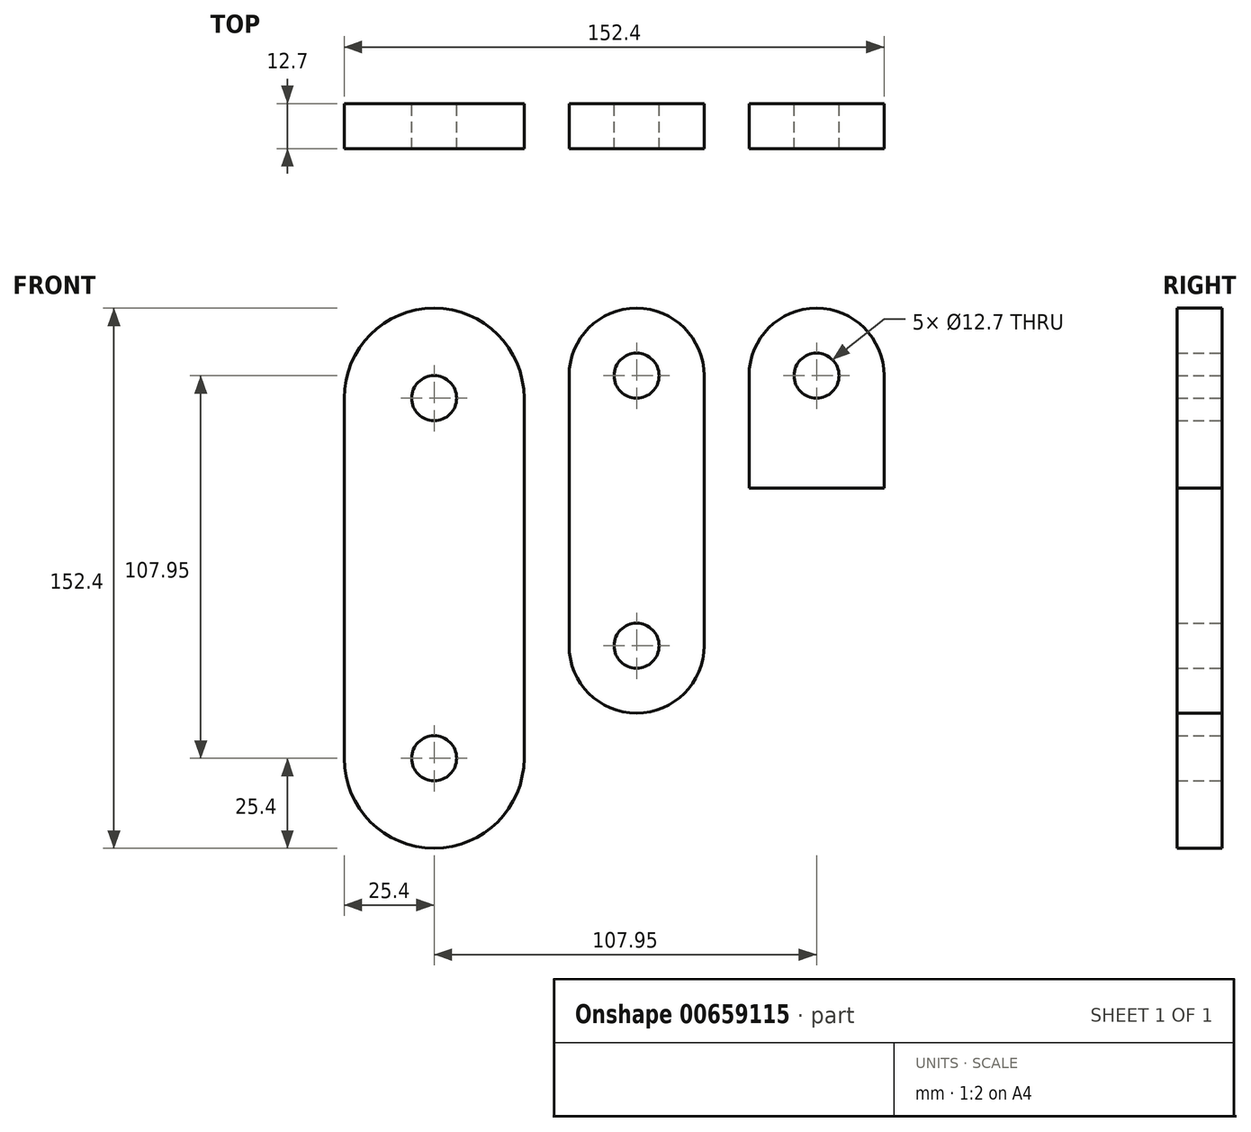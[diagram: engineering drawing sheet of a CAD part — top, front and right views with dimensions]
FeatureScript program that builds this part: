
annotation { "Feature Type Name" : "Feature", "Feature Type Description" : "" }
export const myFeature = defineFeature(function(context is Context, id is Id, definition is map)
    precondition{}
    {
        {
            var Q0;
            Q0=qCreatedBy(makeId("Front.planeOp"),FACE);
            var sketch = newSketch(context, id + "F0", { "sketchPlane" : qUnion([Q0])});
            skArc(sketch, "E0", {"start": v(19.05, 31.75) * mm, "mid": v(0, 50.8) * mm, "end": v(-19.05, 31.75) * mm});
            skCircle(sketch, "E1", {"center": v(0, 31.75) * mm, "radius": 6.35 * mm});
            skLineSegment(sketch, "E2", {"start": v(19.05, 31.75) * mm, "end": v(19.05, 0) * mm});
            skLineSegment(sketch, "E3", {"start": v(-19.05, 0) * mm, "end": v(19.05, 0) * mm});
            skPoint(sketch, "E4.start.orphan", {"position": v(-19.05, 63.5) * mm});
            skPoint(sketch, "E5.center.orphan", {"position": v(0, -25.4) * mm});
            skLineSegment(sketch, "E6", {"start": v(-19.05, 31.75) * mm, "end": v(-19.05, 0) * mm});
            skSolve(sketch);
        }
        {
            var Q0;
            Q0 = qSketchRegion(id + "F0", true);
            extrude(context, id + "F1", {"entities" : qUnion([Q0]), "depth" : 12.7 * mm, "offsetDistance" : 25.4 * mm});
        }
        {
            var Q0;
            Q0=qCreatedBy(makeId("Front.planeOp"),FACE);
            var sketch = newSketch(context, id + "F2", { "sketchPlane" : qUnion([Q0])});
            skCircle(sketch, "E7", {"center": v(-50.8, 31.75) * mm, "radius": 6.35 * mm});
            skArc(sketch, "E8", {"start": v(-31.75, 31.75) * mm, "mid": v(-50.8, 50.8) * mm, "end": v(-69.85, 31.75) * mm});
            skCircle(sketch, "E9", {"center": v(-50.8, -44.45) * mm, "radius": 6.35 * mm});
            skArc(sketch, "E10", {"start": v(-69.85, -44.45) * mm, "mid": v(-50.8, -63.5) * mm, "end": v(-31.75, -44.45) * mm});
            skLineSegment(sketch, "E11", {"start": v(-69.85, 31.75) * mm, "end": v(-69.85, -44.45) * mm});
            skLineSegment(sketch, "E12", {"start": v(-31.75, 31.75) * mm, "end": v(-31.75, -44.45) * mm});
            skSolve(sketch);
        }
        {
            var Q0;
            Q0 = qSketchRegion(id + "F2", true);
            extrude(context, id + "F3", {"entities" : qUnion([Q0]), "depth" : 12.7 * mm, "offsetDistance" : 25.4 * mm});
        }
        {
            var Q0;
            Q0=qCreatedBy(makeId("Front.planeOp"),FACE);
            var sketch = newSketch(context, id + "F4", { "sketchPlane" : qUnion([Q0])});
            skCircle(sketch, "E13", {"center": v(-107.95, 25.4) * mm, "radius": 6.35 * mm});
            skCircle(sketch, "E14", {"center": v(-107.95, -76.2) * mm, "radius": 6.35 * mm});
            skArc(sketch, "E15", {"start": v(-82.55, 25.4) * mm, "mid": v(-107.95, 50.8) * mm, "end": v(-133.35, 25.4) * mm});
            skArc(sketch, "E16", {"start": v(-133.35, -76.2) * mm, "mid": v(-107.95, -101.6) * mm, "end": v(-82.55, -76.2) * mm});
            skLineSegment(sketch, "E17", {"start": v(-133.35, 25.4) * mm, "end": v(-133.35, -76.2) * mm});
            skLineSegment(sketch, "E18", {"start": v(-82.55, 25.4) * mm, "end": v(-82.55, -76.2) * mm});
            skLineSegment(sketch, "E19", {"start": v(-107.95, 50.8) * mm, "end": v(-77.73, 50.8) * mm, "construction": true});
            skSolve(sketch);
        }
        {
            var Q0;
            Q0 = qSketchRegion(id + "F4", true);
            extrude(context, id + "F5", {"entities" : qUnion([Q0]), "depth" : 12.7 * mm, "offsetDistance" : 25.4 * mm});
        }
    });
